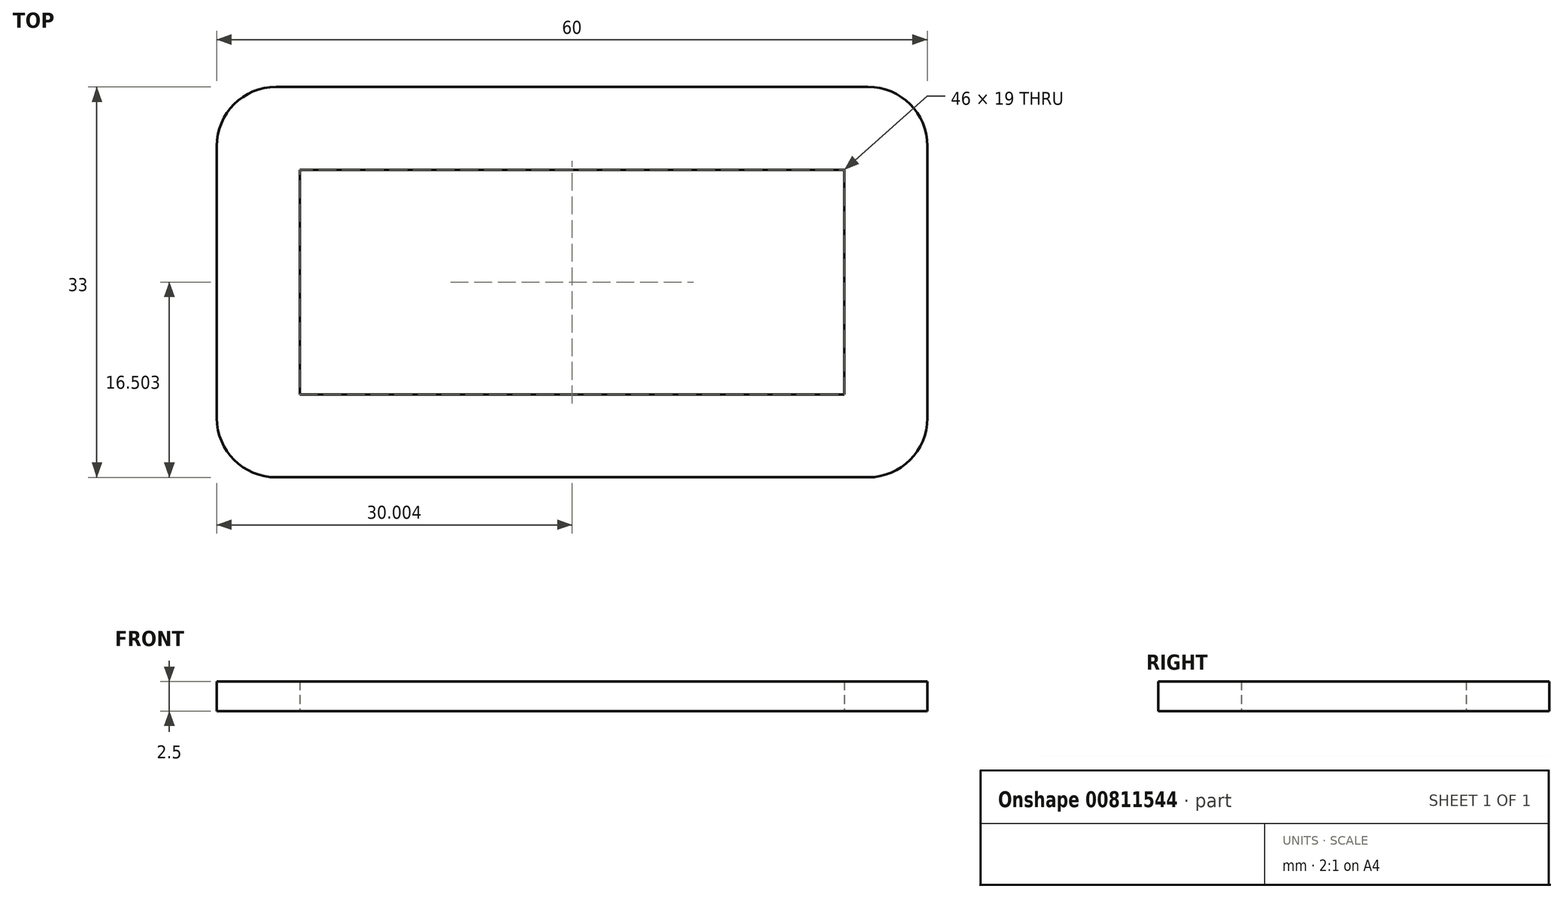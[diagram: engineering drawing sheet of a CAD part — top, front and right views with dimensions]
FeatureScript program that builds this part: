
annotation { "Feature Type Name" : "Feature", "Feature Type Description" : "" }
export const myFeature = defineFeature(function(context is Context, id is Id, definition is map)
    precondition{}
    {
        {
            var Q0;
            Q0=qCreatedBy(makeId("Top.planeOp"),FACE);
            var sketch = newSketch(context, id + "F0", { "sketchPlane" : qUnion([Q0])});
            skLineSegment(sketch, "E0.bottom", {"start": v(-18.8, 11.12) * mm, "end": v(27.2, 11.12) * mm});
            skLineSegment(sketch, "E0.top", {"start": v(-18.8, -7.88) * mm, "end": v(27.2, -7.88) * mm});
            skLineSegment(sketch, "E0.left", {"start": v(-18.8, 11.12) * mm, "end": v(-18.8, -7.88) * mm});
            skLineSegment(sketch, "E0.right", {"start": v(27.2, 11.12) * mm, "end": v(27.2, -7.88) * mm});
            skLineSegment(sketch, "E1.0", {"start": v(34.2, 13.12) * mm, "end": v(34.2, -9.88) * mm});
            skLineSegment(sketch, "E1.1", {"start": v(-20.8, 18.12) * mm, "end": v(29.2, 18.12) * mm});
            skLineSegment(sketch, "E1.2", {"start": v(-25.8, 13.12) * mm, "end": v(-25.8, -9.88) * mm});
            skLineSegment(sketch, "E1.3", {"start": v(-20.8, -14.88) * mm, "end": v(29.2, -14.88) * mm});
            skPoint(sketch, "E2.visualSharp", {"position": v(-25.8, 18.12) * mm});
            skArc(sketch, "E2.filletArc", {"start": v(-20.8, 18.12) * mm, "mid": v(-24.34, 16.66) * mm, "end": v(-25.8, 13.12) * mm});
            skPoint(sketch, "E3.visualSharp", {"position": v(34.2, 18.12) * mm});
            skArc(sketch, "E3.filletArc", {"start": v(34.2, 13.12) * mm, "mid": v(32.73, 16.66) * mm, "end": v(29.2, 18.12) * mm});
            skPoint(sketch, "E4.visualSharp", {"position": v(34.2, -14.88) * mm});
            skArc(sketch, "E4.filletArc", {"start": v(29.2, -14.88) * mm, "mid": v(32.73, -13.41) * mm, "end": v(34.2, -9.88) * mm});
            skPoint(sketch, "E5.visualSharp", {"position": v(-25.8, -14.88) * mm});
            skArc(sketch, "E5.filletArc", {"start": v(-25.8, -9.88) * mm, "mid": v(-24.34, -13.41) * mm, "end": v(-20.8, -14.88) * mm});
            skSolve(sketch);
        }
        {
            var Q0;
            Q0 = qSketchRegion(id + "F0", true);
            extrude(context, id + "F1", {"entities" : qUnion([Q0]), "depth" : 2.5 * mm, "offsetDistance" : 25 * mm});
        }
    });
